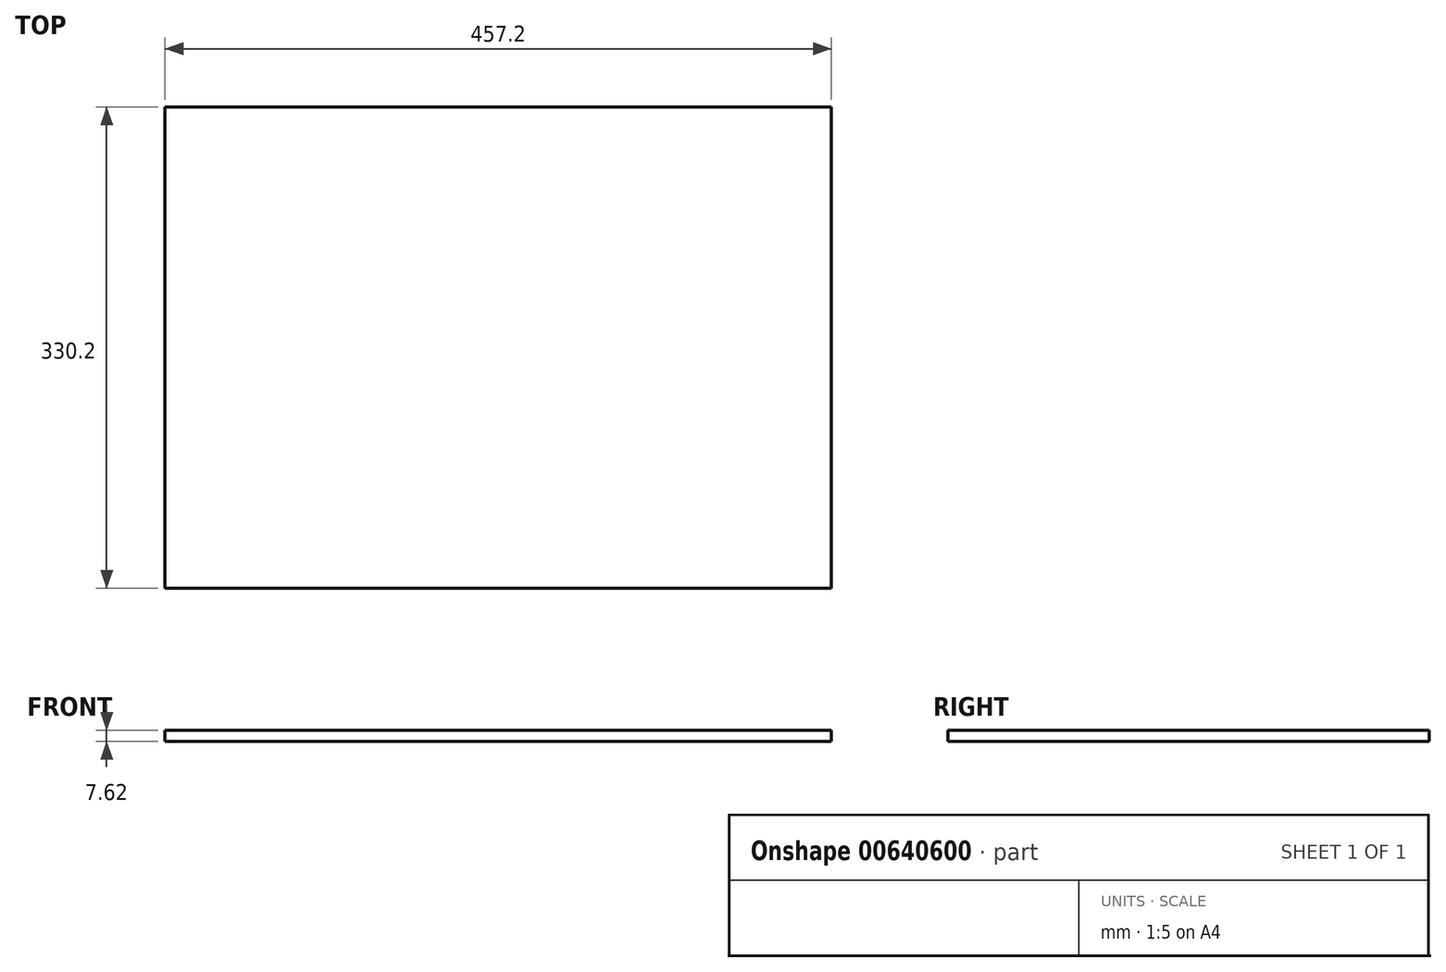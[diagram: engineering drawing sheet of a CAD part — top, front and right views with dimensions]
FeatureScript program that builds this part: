
annotation { "Feature Type Name" : "Feature", "Feature Type Description" : "" }
export const myFeature = defineFeature(function(context is Context, id is Id, definition is map)
    precondition{}
    {
        {
            var Q0;
            Q0=qCreatedBy(makeId("Top.planeOp"),FACE);
            var sketch = newSketch(context, id + "F0", { "sketchPlane" : qUnion([Q0])});
            skLineSegment(sketch, "E0.bottom", {"start": v(-122.28, 253.38) * mm, "end": v(334.92, 253.38) * mm});
            skLineSegment(sketch, "E0.top", {"start": v(-122.28, -76.82) * mm, "end": v(334.92, -76.82) * mm});
            skLineSegment(sketch, "E0.left", {"start": v(-122.28, 253.38) * mm, "end": v(-122.28, -76.82) * mm});
            skLineSegment(sketch, "E0.right", {"start": v(334.92, 253.38) * mm, "end": v(334.92, -76.82) * mm});
            skSolve(sketch);
        }
        {
            var Q0;
            Q0=makeQuery(id+"F0.imprint","IMPRINT",FACE,{"disambiguationData":[TD([[makeQuery(id+"F0.imprint","IMPRINT",EDGE,{"derivedFrom":sQuery(id+"F0.wireOp",EDGE,"E0.bottom")}),-1.0]])]});
            extrude(context, id + "F1", {"entities" : qUnion([Q0]), "depth" : 7.62 * mm, "offsetDistance" : 25.4 * mm});
        }
    });
